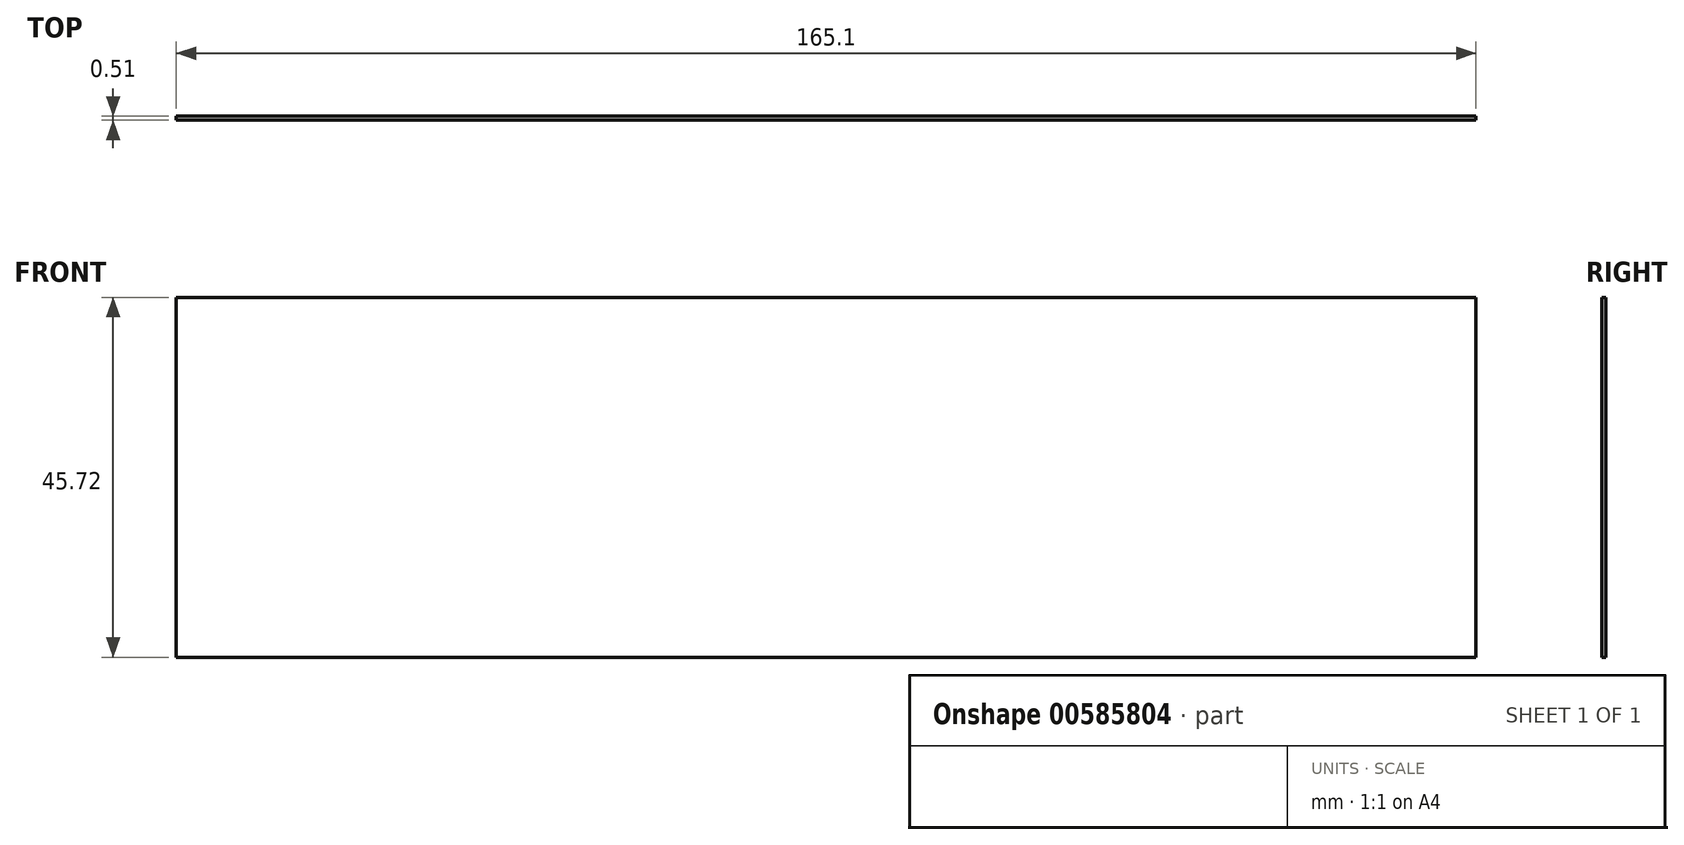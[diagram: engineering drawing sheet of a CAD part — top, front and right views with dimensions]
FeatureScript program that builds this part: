
annotation { "Feature Type Name" : "Feature", "Feature Type Description" : "" }
export const myFeature = defineFeature(function(context is Context, id is Id, definition is map)
    precondition{}
    {
        {
            var Q0;
            Q0=qCreatedBy(makeId("Front.planeOp"),FACE);
            var sketch = newSketch(context, id + "F0", { "sketchPlane" : qUnion([Q0])});
            skLineSegment(sketch, "E0.bottom", {"start": v(82.55, -22.86) * mm, "end": v(-82.55, -22.86) * mm});
            skLineSegment(sketch, "E0.top", {"start": v(82.55, 22.86) * mm, "end": v(-82.55, 22.86) * mm});
            skLineSegment(sketch, "E0.left", {"start": v(82.55, -22.86) * mm, "end": v(82.55, 22.86) * mm});
            skLineSegment(sketch, "E0.right", {"start": v(-82.55, -22.86) * mm, "end": v(-82.55, 22.86) * mm});
            skPoint(sketch, "E0.middle", {"position": v(0, 0) * mm});
            skSolve(sketch);
        }
        {
            var Q0;
            Q0=makeQuery(id+"F0.imprint","IMPRINT",FACE,{"disambiguationData":[TD([[makeQuery(id+"F0.imprint","IMPRINT",EDGE,{"derivedFrom":sQuery(id+"F0.wireOp",EDGE,"E0.bottom")}),-1.0]])]});
            extrude(context, id + "F1", {"entities" : qUnion([Q0]), "depth" : 0.5 * mm, "offsetDistance" : 25.4 * mm});
        }
    });
